# Revit family: HUNTER_PROS04-PRS30
name_source: partatom
category: Sprinklers
revit_build: Autodesk Revit 2017 (Build: 20160225_1515(x64)
units: mm (PartAtom-declared; Revit-internal decimal feet)

## family parameters
Always vertical = Yes
Cut with Voids When Loaded = No
Maintain Annotation Orientation = No
OmniClass Number = 23.11.27.15.11.11
OmniClass Title = Installed Sprinkler Heads
Part Type = Normal
Room Calculation Point = No
Round Connector Dimension = Use Diameter
Shared = Yes
Work Plane-Based = No

## types (11) — shared parameters
Arc Max = 360.00°
Assembly Code = G2050700
Body Height = 155 mm
Body Material = Hunter® ABS Plastic
Connection_Dia = 15 mm  [stored 0.0492126 ft]
Diameter = 610 mm
Exposed Diameter = 57 mm
Inlet Size = 1/2" NPT
Keynote = 328423.02
Manufacturer = Hunter® Industries
Nozzle_URL = https://www.hunterindustries.com
Pop Up Height = 100 mm  [stored 0.328084 ft]
Pop Up Material = Hunter® ABS Plastic
Pressure = 210.0 kPa
Seal = Hunter® White Flex Seal
Show 2D Symbol = Yes
Show Water Spray = Yes
Type Comments = Pro-Spray® PROS-04
Type Image = <None>
URL = https://www.hunterindustries.com
Water = Water

## per-type parameters (varying)
| type | Annotation Symbol | Arc Min | Description | Model | Nozzle Size | Nozzle_Ref | Trajectory Angle | Trajectory Radius |
| PROS-04-PRS30-4A_Lt. Green_1.2m | Nozzle 4A | 0.00° | ProSpray® with Pressure Regulator PROS-04-PRS30 10cm PopUp and Pro Adjustable 4A-Lt. Green Nozzle | PROS-04-PRS30-4A | Hunter® Pro Adjustable (4A) Lt.Green Nozzle | 4 | 3.00° | 1200 mm  [stored 3.93701 ft] |
| PROS-04-PRS30-6A_Lt. Blue_1.8m | Nozzle 6A | 0.00° | ProSpray® with Pressure Regulator PROS-04-PRS30 10cm PopUp and Pro Adjustable 6A-Lt. Blue Nozzle | PROS-04-PRS30-6A | Hunter® Pro Adjustable (6A) Lt.Blue Nozzle | 6 | 3.00° | 1800 mm |
| PROS-04-PRS30-8A_Brown_2.4m | Nozzle 8A | 0.00° | ProSpray® with Pressure Regulator PROS-04-PRS30 10cm PopUp and Pro Adjustable 8A-Brown Nozzle | PROS-04-PRS30-8A | Hunter® Pro Adjustable (8A) Brown Nozzle | 8 | 3.00° | 2400 mm |
| PROS-04-PRS30-10A_Red_3.0m | Nozzle 10A | 0.00° | ProSpray® with Pressure Regulator PROS-04-PRS30 10cm PopUp and Pro Adjustable 10A-Red Nozzle | PROS-04-PRS30-10A | Hunter® Pro Adjustable (10A) Red Nozzle | 10 | 15.00° | 3000 mm  [stored 9.84252 ft] |
| PROS-04-PRS30-12A_Green_3.7m | Nozzle 12A | 0.00° | ProSpray® with Pressure Regulator PROS-04-PRS30 10cm PopUp and Pro Adjustable 12A-Green Nozzle | PROS-04-PRS30-12A | Hunter® Pro Adjustable (12A) Green Nozzle | 12 | 28.00° | 3700 mm |
| PROS-04-PRS30-15A_Black_4.6m | Nozzle 15A | 0.00° | ProSpray® with Pressure Regulator PROS-04-PRS30 10cm PopUp and Pro Adjustable 15A-Black Nozzle | PROS-04-PRS30-15A | Hunter® Pro Adjustable (15A) Black Nozzle | 15 | 28.00° | 4600 mm |
| PROS-04-PRS30-17A_Grey_5.2m | Nozzle 17A | 0.00° | ProSpray® with Pressure Regulator PROS-04-PRS30 10cm PopUp and Pro Adjustable 17A-Grey Nozzle | PROS-04-PRS30-17A | Hunter® Pro Adjustable (17A) Grey Nozzle | 17 | 28.00° | 5200 mm |
| PROS-04-PRS30-PCN10_Red | PCN10 | 45.00° | ProSpray® with Pressure Regulator PROS-04-PRS30 10cm PopUp with Pressure Compensating Bubbler Nozzle PCN-10 Red | PROS-04-PRS30-PCN-10 | Hunter®Pressure Compensating Bubbler Nozzles (PCN-10) Red Nozzle | 3010 | 10.00° | 450 mm  [stored 1.47638 ft] |
| PROS-04-PRS30-PCN20_Yellow | PCN20 | 45.00° | ProSpray® with Pressure Regulator PROS-04-PRS30 10cm PopUp with Pressure Compensating Bubbler Nozzle PCN-20 Yellow | PROS-04-PRS30-PCN-20 | Hunter®Pressure Compensating Bubbler Nozzles (PCN-20) Yellow Nozzle | 3020 | 10.00° | 450 mm  [stored 1.47638 ft] |
| PROS-04-PRS30-PCN25_Lt.Blue | PCN25 | 45.00° | PProSpray® with Pressure Regulator PROS-04-PRS30 10cm PopUp with Pressure Compensating Bubbler Nozzle PCN-25 Lt.Blue | PROS-04-PRS30-PCN25 | Hunter®Pressure Compensating Bubbler Nozzles (PCN-25) Lt.Blue Nozzle | 3025 | 10.00° | 450 mm  [stored 1.47638 ft] |
| PROS-04-PRS30-PCN50_Lt.Green | PCN50 | 45.00° | ProSpray® with Pressure Regulator PROS-04-PRS30 10cm PopUp with Pressure Compensating Bubbler Nozzle PCN-50 Lt.Green | PROS-04-PRS30-PCN50 | Hunter®Pressure Compensating Bubbler Nozzles (PCN-50) Lt.Green Nozzle | 3050 | 10.00° | 450 mm  [stored 1.47638 ft] |

note: [stored X ft] marks values corroborated as IEEE doubles in the binary element streams (Revit-internal decimal feet)

## geometry (parser evidence)
native form markers: Sweep x29
no freeform markers — native parametric forms only
